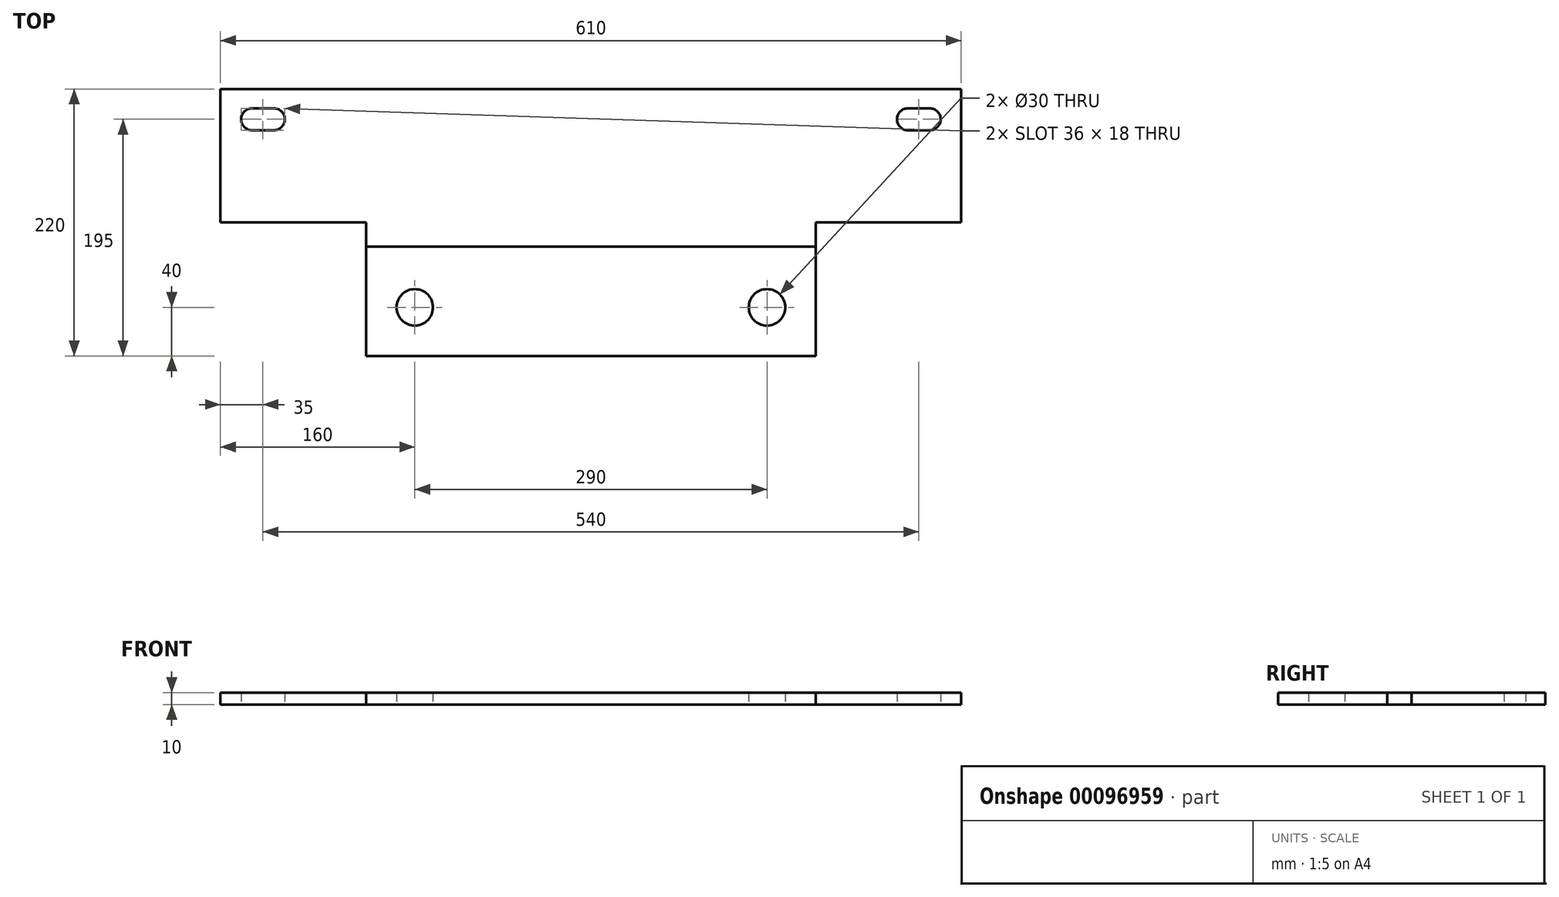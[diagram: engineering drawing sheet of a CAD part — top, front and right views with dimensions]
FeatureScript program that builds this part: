
annotation { "Feature Type Name" : "Feature", "Feature Type Description" : "" }
export const myFeature = defineFeature(function(context is Context, id is Id, definition is map)
    precondition{}
    {
        {
            var Q0;
            Q0=qCreatedBy(makeId("Top.planeOp"),FACE);
            var sketch = newSketch(context, id + "F0", { "sketchPlane" : qUnion([Q0])});
            skLineSegment(sketch, "E0", {"start": v(0, 0) * mm, "end": v(-305, 0) * mm});
            skLineSegment(sketch, "E1", {"start": v(-305, 0) * mm, "end": v(-305, 110) * mm});
            skLineSegment(sketch, "E2", {"start": v(-305, 110) * mm, "end": v(0, 110) * mm});
            skLineSegment(sketch, "E3", {"start": v(-185, 0) * mm, "end": v(-185, -110) * mm});
            skLineSegment(sketch, "E4", {"start": v(-185, -110) * mm, "end": v(0, -110) * mm});
            skLineSegment(sketch, "E5", {"start": v(-185, -20) * mm, "end": v(0, -20) * mm});
            skLineSegment(sketch, "E6", {"start": v(-270, 110) * mm, "end": v(-270, 0) * mm, "construction": true});
            skPoint(sketch, "E7", {"position": v(-270, 85) * mm});
            skLineSegment(sketch, "E8.bottom", {"start": v(-261, 94) * mm, "end": v(-279, 94) * mm});
            skLineSegment(sketch, "E8.top", {"start": v(-261, 76) * mm, "end": v(-279, 76) * mm});
            skLineSegment(sketch, "E8.left", {"start": v(-261, 94) * mm, "end": v(-261, 76) * mm});
            skLineSegment(sketch, "E8.right", {"start": v(-279, 94) * mm, "end": v(-279, 76) * mm});
            skCircle(sketch, "E9", {"center": v(-261, 85) * mm, "radius": 9 * mm});
            skCircle(sketch, "E10", {"center": v(-279, 85) * mm, "radius": 9 * mm});
            skLineSegment(sketch, "E11", {"start": v(-145, -110) * mm, "end": v(-145, -20) * mm, "construction": true});
            skPoint(sketch, "E12", {"position": v(-145, -70) * mm});
            skLineSegment(sketch, "E13.MirrorCS", {"start": v(261, 76) * mm, "end": v(279, 76) * mm});
            skLineSegment(sketch, "E14.MirrorCS", {"start": v(279, 94) * mm, "end": v(279, 76) * mm});
            skPoint(sketch, "E15.MirrorP", {"position": v(270, 85) * mm});
            skLineSegment(sketch, "E16.MirrorCS", {"start": v(261, 94) * mm, "end": v(261, 76) * mm});
            skLineSegment(sketch, "E17.MirrorCS", {"start": v(261, 94) * mm, "end": v(279, 94) * mm});
            skLineSegment(sketch, "E18.MirrorCS", {"start": v(185, -20) * mm, "end": v(0, -20) * mm});
            skLineSegment(sketch, "E19.MirrorCS", {"start": v(185, 0) * mm, "end": v(185, -110) * mm});
            skLineSegment(sketch, "E20.MirrorCS", {"start": v(270, 110) * mm, "end": v(270, 0) * mm, "construction": true});
            skLineSegment(sketch, "E21.MirrorCS", {"start": v(305, 0) * mm, "end": v(305, 110) * mm});
            skLineSegment(sketch, "E22.MirrorCS", {"start": v(305, 110) * mm, "end": v(0, 110) * mm});
            skLineSegment(sketch, "E23.MirrorCS", {"start": v(0, 0) * mm, "end": v(305, 0) * mm});
            skCircle(sketch, "E24.MirrorC", {"center": v(261, 85) * mm, "radius": 9 * mm});
            skPoint(sketch, "E25.MirrorP", {"position": v(145, -70) * mm});
            skLineSegment(sketch, "E26.MirrorCS", {"start": v(185, -110) * mm, "end": v(0, -110) * mm});
            skLineSegment(sketch, "E27.MirrorCS", {"start": v(145, -110) * mm, "end": v(145, -20) * mm, "construction": true});
            skCircle(sketch, "E28.MirrorC", {"center": v(279, 85) * mm, "radius": 9 * mm});
            skSolve(sketch);
        }
        {
            var Q0;
            {var subQ12=sQuery(id+"F0.wireOp",EDGE,"E1");Q0=makeQuery(id+"F0.imprint","IMPRINT",FACE,{"disambiguationData":[TD([[makeQuery(id+"F0.imprint","IMPRINT",EDGE,{"derivedFrom":subQ12}),-1.0]])]});}
            var Q1;
            {var subQ6=sQuery(id+"F0.wireOp",EDGE,"E5");Q1=makeQuery(id+"F0.imprint","IMPRINT",FACE,{"disambiguationData":[TD([[makeQuery(id+"F0.imprint","IMPRINT",EDGE,{"derivedFrom":subQ6}),1.0]])]});}
            extrude(context, id + "F1", {"entities" : qUnion([Q0, Q1]), "depth" : 10 * mm, "offsetDistance" : 25 * mm});
        }
        {
            var Q0;
            {var subQ2=sQuery(id+"F0.wireOp",EDGE,"E4");Q0=makeQuery(id+"F0.imprint","IMPRINT",FACE,{"disambiguationData":[TD([[makeQuery(id+"F0.imprint","IMPRINT",EDGE,{"derivedFrom":subQ2}),1.0]])]});}
            extrude(context, id + "F2", {"entities" : qUnion([Q0]), "depth" : 10 * mm, "offsetDistance" : 25 * mm});
        }
        {
            var Q0;
            Q0=sQuery(id+"F0.wireOp",VERTEX,"E12");
            var Q1;
            Q1=sQuery(id+"F0.wireOp",VERTEX,"E25.MirrorP");
            var Q2;
            Q2=makeQuery(id+"F2.opExtrude","SWEPT_BODY",BODY,{"disambiguationData":[OSD([sQuery(id+"F0.wireOp",EDGE,"E3"),sQuery(id+"F0.wireOp",EDGE,"E4"),sQuery(id+"F0.wireOp",EDGE,"E5"),sQuery(id+"F0.wireOp",EDGE,"E18.MirrorCS"),sQuery(id+"F0.wireOp",EDGE,"E19.MirrorCS"),sQuery(id+"F0.wireOp",EDGE,"E26.MirrorCS")])]});
            hole(context, id + "F3", {"style" : HoleStyle.SIMPLE, "endStyle" : HoleEndStyle.THROUGH, "oppositeDirection" : true, "holeDiameter" : 30 * mm, "majorDiameter" : 5 * mm, "tappedDepth" : 12 * mm, "tapClearance" : 3, "locations" : qUnion([Q0, Q1]), "scope" : qUnion([Q2])});
        }
    });
